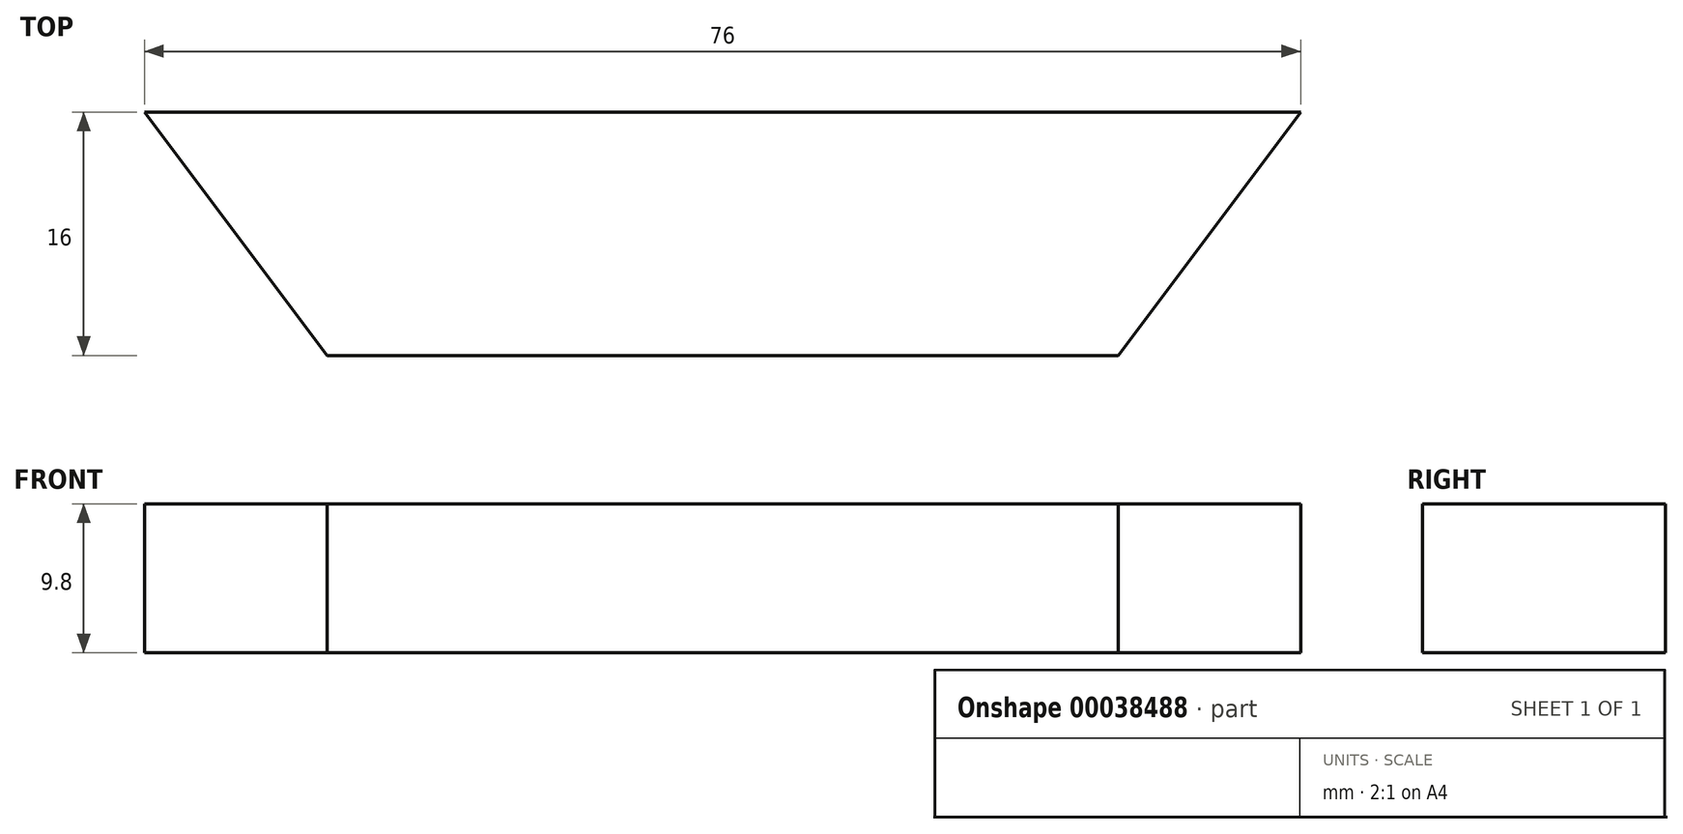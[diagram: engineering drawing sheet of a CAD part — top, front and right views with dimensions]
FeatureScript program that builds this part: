
annotation { "Feature Type Name" : "Feature", "Feature Type Description" : "" }
export const myFeature = defineFeature(function(context is Context, id is Id, definition is map)
    precondition{}
    {
        {
            var Q0;
            Q0=qCreatedBy(makeId("Top.planeOp"),FACE);
            var sketch = newSketch(context, id + "F0", { "sketchPlane" : qUnion([Q0])});
            skLineSegment(sketch, "E0", {"start": v(-46.12, 37.64) * mm, "end": v(29.88, 37.64) * mm});
            skLineSegment(sketch, "E1", {"start": v(-46.12, 37.64) * mm, "end": v(-34.12, 21.64) * mm});
            skLineSegment(sketch, "E2", {"start": v(-34.12, 21.64) * mm, "end": v(17.88, 21.64) * mm});
            skLineSegment(sketch, "E3", {"start": v(29.88, 37.64) * mm, "end": v(17.88, 21.64) * mm});
            skLineSegment(sketch, "E4", {"start": v(-12.76, 37.64) * mm, "end": v(-12.76, 21.64) * mm});
            skSolve(sketch);
        }
        {
            var Q0;
            {var subQ2=sQuery(id+"F0.wireOp",EDGE,"E1");Q0=makeQuery(id+"F0.imprint","IMPRINT",FACE,{"disambiguationData":[TD([[makeQuery(id+"F0.imprint","IMPRINT",EDGE,{"derivedFrom":subQ2}),1.0]])]});}
            var Q1;
            {var subQ1=sQuery(id+"F0.wireOp",EDGE,"E3");Q1=makeQuery(id+"F0.imprint","IMPRINT",FACE,{"disambiguationData":[TD([[makeQuery(id+"F0.imprint","IMPRINT",EDGE,{"derivedFrom":subQ1}),-1.0]])]});}
            extrude(context, id + "F1", {"entities" : qUnion([Q0, Q1]), "depth" : 9.8 * mm});
        }
    });
